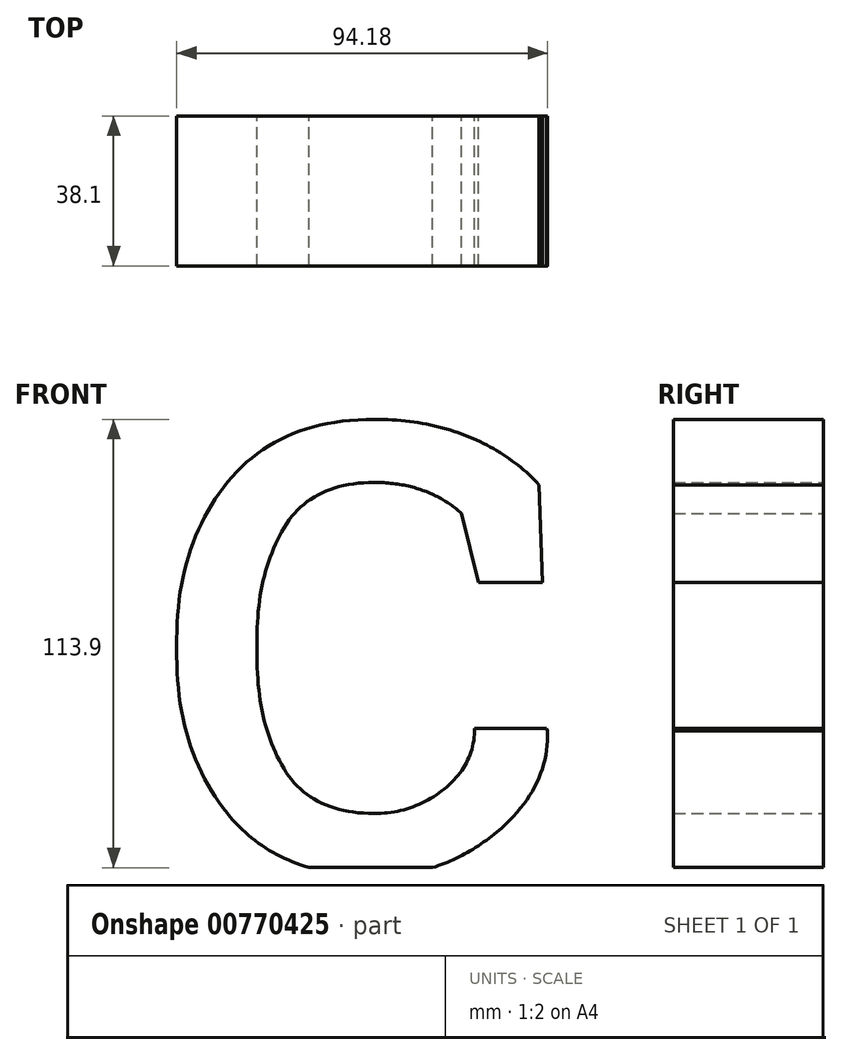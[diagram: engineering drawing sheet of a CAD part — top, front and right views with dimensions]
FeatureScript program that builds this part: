
annotation { "Feature Type Name" : "Feature", "Feature Type Description" : "" }
export const myFeature = defineFeature(function(context is Context, id is Id, definition is map)
    precondition{}
    {
        {
            var Q0;
            Q0=qCreatedBy(makeId("Front.planeOp"),FACE);
            var sketch = newSketch(context, id + "F0", { "sketchPlane" : qUnion([Q0])});
            skText(sketch, "E0", { "text": "c", "fontName": "RobotoSlab-Regular.ttf"});
            const initialGuessF0  = {"E0": [-0.14193, -0.03852, 1, 0, 0.1524]};
            skSetInitialGuess(sketch, initialGuessF0);
            skSolve(sketch);
        }
        {
            var Q0;
            Q0 = qSketchRegion(id + "F0", true);
            extrude(context, id + "F1", {"entities" : qUnion([Q0]), "depth" : 38.1 * mm, "offsetDistance" : 25 * mm});
        }
        {
            var Q0;
            Q0=makeQuery(id+"F1.opExtrude","SWEPT_FACE",FACE,{"disambiguationData":[OSD([sQuery(id+"F0.wireOp",EDGE,"E0.sketch_text.stroke-2")])]});
            cPlane(context, id + "F2", {"entities" : qUnion([Q0]), "cplaneType" : CPlaneType.OFFSET, "offset" : 35.35 * mm, "oppositeDirection" : true, "width" : 150 * mm, "height" : 150 * mm});
        }
        {
            var Q0;
            Q0=qCreatedBy(id+"F2.planeOp",FACE);
            var sketch = newSketch(context, id + "F3", { "sketchPlane" : qUnion([Q0])});
            skLineSegment(sketch, "E1.bottom", {"start": v(-148.63, -52.14) * mm, "end": v(-13.02, -52.14) * mm});
            skLineSegment(sketch, "E1.top", {"start": v(-148.63, 19.06) * mm, "end": v(-13.02, 19.06) * mm});
            skLineSegment(sketch, "E1.left", {"start": v(-148.63, -52.14) * mm, "end": v(-148.63, 19.06) * mm});
            skLineSegment(sketch, "E1.right", {"start": v(-13.02, -52.14) * mm, "end": v(-13.02, 19.06) * mm});
            skSolve(sketch);
        }
        {
            var Q0;
            Q0=makeQuery(id+"F3.imprint","IMPRINT",FACE,{"disambiguationData":[TD([[makeQuery(id+"F3.imprint","IMPRINT",EDGE,{"derivedFrom":sQuery(id+"F3.wireOp",EDGE,"E1.bottom")}),1.0]])]});
            extrude(context, id + "F4", {"entities" : qUnion([Q0]), "operationType" : NewBodyOperationType.REMOVE, "oppositeDirection" : true, "depth" : 25 * mm, "offsetDistance" : 25 * mm});
        }
    });
